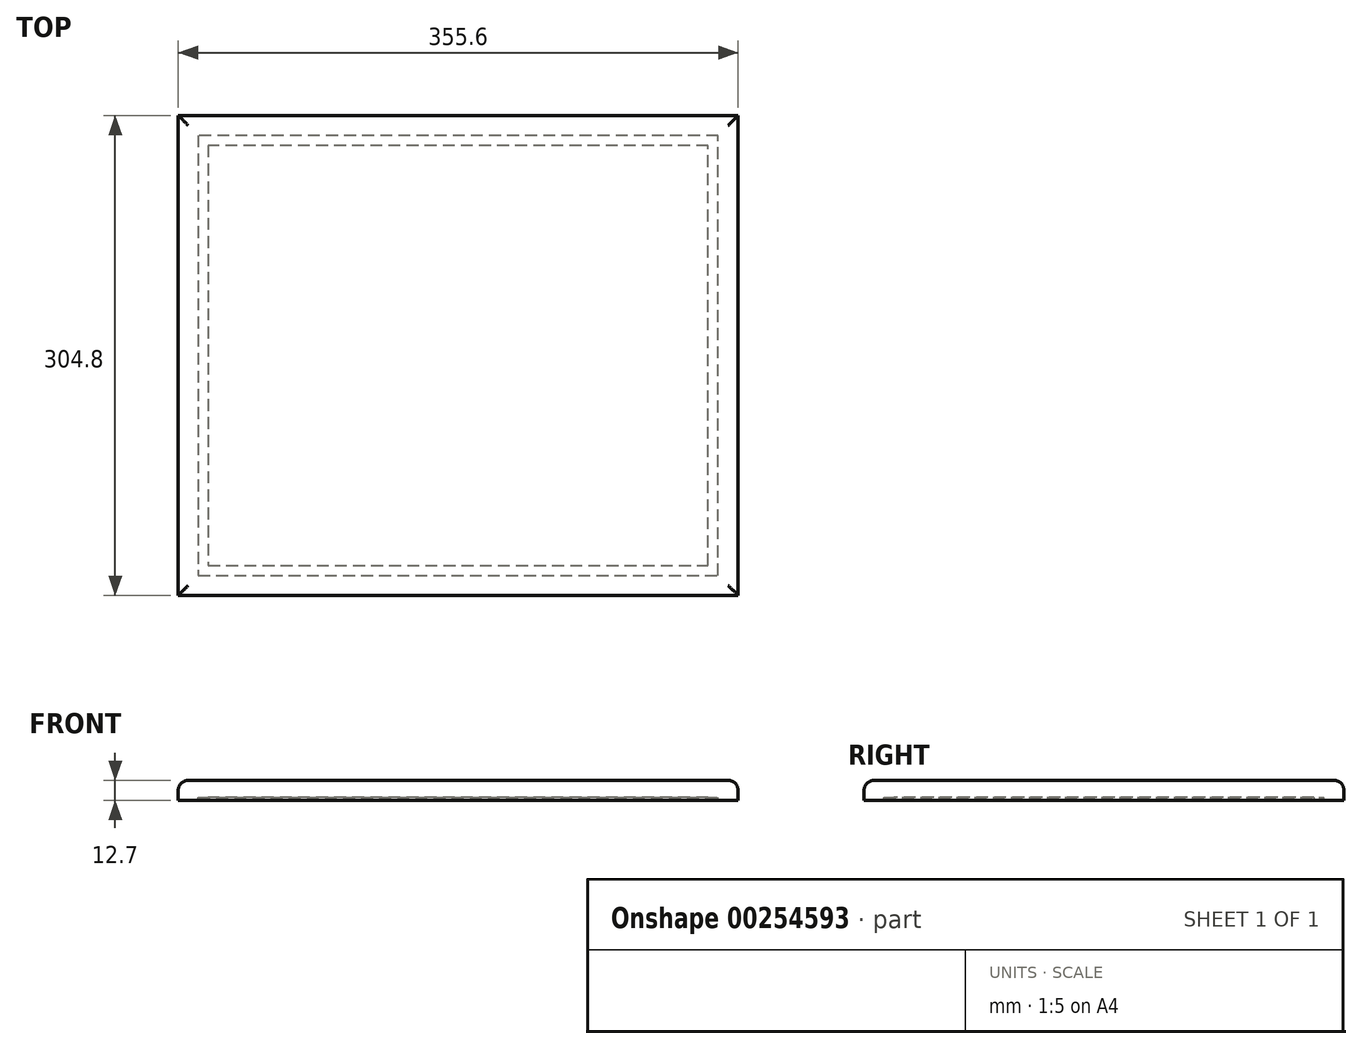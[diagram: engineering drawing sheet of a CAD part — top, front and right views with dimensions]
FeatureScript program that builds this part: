
annotation { "Feature Type Name" : "Feature", "Feature Type Description" : "" }
export const myFeature = defineFeature(function(context is Context, id is Id, definition is map)
    precondition{}
    {
        {
            var Q0;
            Q0=qCreatedBy(makeId("Top.planeOp"),FACE);
            var sketch = newSketch(context, id + "F0", { "sketchPlane" : qUnion([Q0])});
            skLineSegment(sketch, "E0.bottom", {"start": v(0, 0) * mm, "end": v(355.6, 0) * mm});
            skLineSegment(sketch, "E0.top", {"start": v(0, -304.8) * mm, "end": v(355.6, -304.8) * mm});
            skLineSegment(sketch, "E0.left", {"start": v(0, 0) * mm, "end": v(0, -304.8) * mm});
            skLineSegment(sketch, "E0.right", {"start": v(355.6, 0) * mm, "end": v(355.6, -304.8) * mm});
            skSolve(sketch);
        }
        {
            var Q0;
            Q0 = qSketchRegion(id + "F0", true);
            extrude(context, id + "F1", {"entities" : qUnion([Q0]), "depth" : 12.7 * mm});
        }
        {
            var Q0;
            Q0=makeQuery(id+"F1.opExtrude","CAP_EDGE",EDGE,{"disambiguationData":[OSD([sQuery(id+"F0.wireOp",EDGE,"E0.left")])],"isStart":false});
            var Q1;
            Q1=makeQuery(id+"F1.opExtrude","CAP_EDGE",EDGE,{"disambiguationData":[OSD([sQuery(id+"F0.wireOp",EDGE,"E0.top")])],"isStart":false});
            var Q2;
            Q2=makeQuery(id+"F1.opExtrude","CAP_EDGE",EDGE,{"disambiguationData":[OSD([sQuery(id+"F0.wireOp",EDGE,"E0.right")])],"isStart":false});
            var Q3;
            Q3=makeQuery(id+"F1.opExtrude","CAP_EDGE",EDGE,{"disambiguationData":[OSD([sQuery(id+"F0.wireOp",EDGE,"E0.bottom")])],"isStart":false});
            fillet(context, id + "F2", {"entities" : qUnion([Q0, Q1, Q2, Q3]), "radius" : 6.35 * mm, "tangentPropagation" : true, "allowEdgeOverflow" : false});
        }
        {
            var Q0;
            Q0=makeQuery(id+"F1.opExtrude","CAP_FACE",FACE,{"disambiguationData":[OSD([sQuery(id+"F0.wireOp",EDGE,"E0.bottom"),sQuery(id+"F0.wireOp",EDGE,"E0.top"),sQuery(id+"F0.wireOp",EDGE,"E0.left"),sQuery(id+"F0.wireOp",EDGE,"E0.right")])],"isStart":true});
            var sketch = newSketch(context, id + "F3", { "sketchPlane" : qUnion([Q0])});
            skLineSegment(sketch, "E1.bottom", {"start": v(12.7, 292.1) * mm, "end": v(342.9, 292.1) * mm});
            skLineSegment(sketch, "E1.top", {"start": v(12.7, 12.7) * mm, "end": v(342.9, 12.7) * mm});
            skLineSegment(sketch, "E1.left", {"start": v(12.7, 292.1) * mm, "end": v(12.7, 12.7) * mm});
            skLineSegment(sketch, "E1.right", {"start": v(342.9, 292.1) * mm, "end": v(342.9, 12.7) * mm});
            skSolve(sketch);
        }
        {
            var Q0;
            Q0=qCreatedBy(makeId("Front.planeOp"),FACE);
            var Q1;
            Q1=sQuery(id+"F3.wireOp",VERTEX,"E1.left.end");
            cPlane(context, id + "F4", {"entities" : qUnion([Q0, Q1]), "cplaneType" : CPlaneType.PLANE_POINT, "offset" : 25.4 * mm, "width" : 152.4 * mm, "height" : 152.4 * mm});
        }
        {
            var Q0;
            Q0=qCreatedBy(id+"F4.planeOp",FACE);
            var sketch = newSketch(context, id + "F5", { "sketchPlane" : qUnion([Q0])});
            skLineSegment(sketch, "E2.bottom", {"start": v(12.7, 0) * mm, "end": v(19.05, 0) * mm});
            skLineSegment(sketch, "E2.top", {"start": v(12.7, 2.03) * mm, "end": v(19.05, 2.03) * mm});
            skLineSegment(sketch, "E2.left", {"start": v(12.7, 0) * mm, "end": v(12.7, 2.03) * mm});
            skLineSegment(sketch, "E2.right", {"start": v(19.05, 0) * mm, "end": v(19.05, 2.03) * mm});
            skSolve(sketch);
        }
        {
            var Q0;
            Q0 = qSketchRegion(id + "F5", true);
            var Q1;
            Q1=sQuery(id+"F3.wireOp",EDGE,"E1.left");
            var Q2;
            Q2=sQuery(id+"F3.wireOp",EDGE,"E1.bottom");
            var Q3;
            Q3=sQuery(id+"F3.wireOp",EDGE,"E1.top");
            var Q4;
            Q4=sQuery(id+"F3.wireOp",EDGE,"E1.right");
            sweep(context, id + "F6", {"operationType" : NewBodyOperationType.REMOVE, "profiles" : qUnion([Q0]), "path" : qUnion([Q1, Q2, Q3, Q4])});
        }
    });
